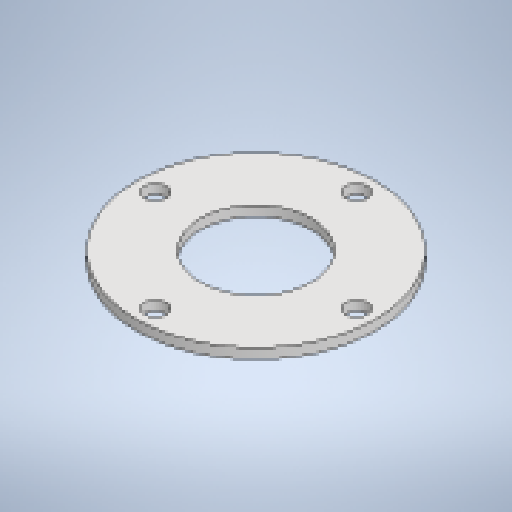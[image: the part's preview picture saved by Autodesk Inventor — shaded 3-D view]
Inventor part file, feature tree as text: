
AUTODESK INVENTOR PART (.ipt)
format: ipt  version: 2025 (Build 290162010, 162A)  size: 195,072 bytes
history: native  units: mm
features: other x3, sketch x2, sheet_metal_op x1, pattern_circular x1
ambient origin geometry x8: Origin, YZ Plane, XZ Plane, XY Plane, X Axis, Y Axis, Z Axis, Center Point
bodies: Body1 (feature_tree)
feature tree (7):
  sheet_metal_op  "Face2"
  pattern_circular  "Circular Pattern1"  [2 undecoded]
  sketch  "Sketch2"  dims[d14=8.0mm]
  other  "Plate2"
  sketch  "Sketch3"  dims[d15=17.0mm d17=8.0mm d18=0.0mm d19=40.0mm d20=360.0deg d25=91.0mm d27=190.0mm d28=160.0mm]
  other  "Cut1"
  other  "Definition1"
note: 2 required parameter values undecoded (feature->parameter linkage not recoverable at this tier; creation-order binding heuristic only, values carry confidence <= 0.55)
